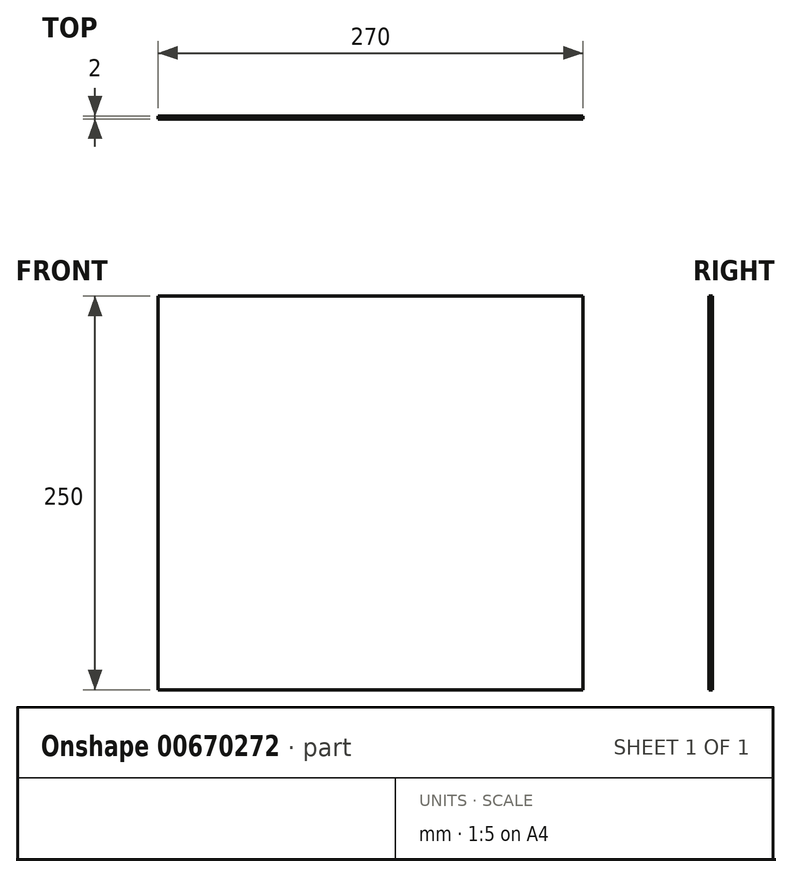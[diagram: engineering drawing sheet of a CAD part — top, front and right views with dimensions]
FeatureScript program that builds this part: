
annotation { "Feature Type Name" : "Feature", "Feature Type Description" : "" }
export const myFeature = defineFeature(function(context is Context, id is Id, definition is map)
    precondition{}
    {
        {
            var Q0;
            Q0=qCreatedBy(makeId("Front.planeOp"),FACE);
            var sketch = newSketch(context, id + "F0", { "sketchPlane" : qUnion([Q0])});
            skLineSegment(sketch, "E0.bottom", {"start": v(-134.83, 105.9) * mm, "end": v(135.17, 105.9) * mm});
            skLineSegment(sketch, "E0.top", {"start": v(-134.83, -144.1) * mm, "end": v(135.17, -144.1) * mm});
            skLineSegment(sketch, "E0.left", {"start": v(-134.83, 105.9) * mm, "end": v(-134.83, -144.1) * mm});
            skLineSegment(sketch, "E0.right", {"start": v(135.17, 105.9) * mm, "end": v(135.17, -144.1) * mm});
            skSolve(sketch);
        }
        {
            var Q0;
            Q0=makeQuery(id+"F0.imprint","IMPRINT",FACE,{"disambiguationData":[TD([[makeQuery(id+"F0.imprint","IMPRINT",EDGE,{"derivedFrom":sQuery(id+"F0.wireOp",EDGE,"E0.bottom")}),-1.0]])]});
            extrude(context, id + "F1", {"entities" : qUnion([Q0]), "depth" : 2 * mm, "offsetDistance" : 25 * mm});
        }
    });
